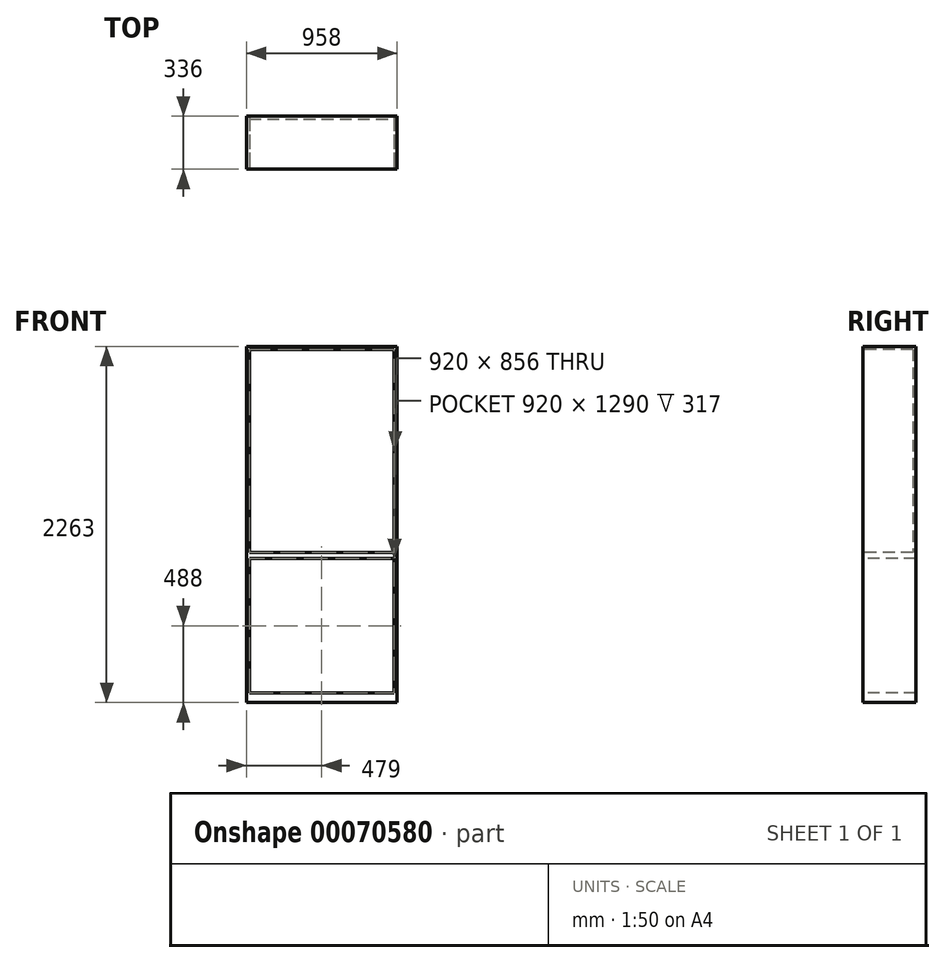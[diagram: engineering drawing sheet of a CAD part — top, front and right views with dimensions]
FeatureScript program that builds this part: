
annotation { "Feature Type Name" : "Feature", "Feature Type Description" : "" }
export const myFeature = defineFeature(function(context is Context, id is Id, definition is map)
    precondition{}
    {
        {
            var Q0;
            Q0=qCreatedBy(makeId("Front.planeOp"),FACE);
            var sketch = newSketch(context, id + "F0", { "sketchPlane" : qUnion([Q0])});
            skLineSegment(sketch, "E0.bottom", {"start": v(0, 0) * mm, "end": v(958, 0) * mm});
            skLineSegment(sketch, "E0.top", {"start": v(0, 2263) * mm, "end": v(958, 2263) * mm});
            skLineSegment(sketch, "E0.left", {"start": v(0, 0) * mm, "end": v(0, 2263) * mm});
            skLineSegment(sketch, "E0.right", {"start": v(958, 0) * mm, "end": v(958, 2263) * mm});
            skSolve(sketch);
        }
        {
            var Q0;
            Q0=makeQuery(id+"F0.imprint","IMPRINT",FACE,{"disambiguationData":[TD([[makeQuery(id+"F0.imprint","IMPRINT",EDGE,{"derivedFrom":sQuery(id+"F0.wireOp",EDGE,"E0.bottom")}),1.0]])]});
            extrude(context, id + "F1", {"entities" : qUnion([Q0]), "depth" : (355 - 19) * mm});
        }
        {
            var Q0;
            Q0=makeQuery(id+"F1.opExtrude","CAP_FACE",FACE,{"disambiguationData":[OSD([sQuery(id+"F0.wireOp",EDGE,"E0.bottom"),sQuery(id+"F0.wireOp",EDGE,"E0.top"),sQuery(id+"F0.wireOp",EDGE,"E0.left"),sQuery(id+"F0.wireOp",EDGE,"E0.right")])],"isStart":false});
            var sketch = newSketch(context, id + "F2", { "sketchPlane" : qUnion([Q0])});
            skLineSegment(sketch, "E1.bottom", {"start": v(19, 916) * mm, "end": v(939, 916) * mm});
            skLineSegment(sketch, "E1.top", {"start": v(19, 60) * mm, "end": v(939, 60) * mm});
            skLineSegment(sketch, "E1.left", {"start": v(19, 916) * mm, "end": v(19, 60) * mm});
            skLineSegment(sketch, "E1.right", {"start": v(939, 916) * mm, "end": v(939, 60) * mm});
            skLineSegment(sketch, "E2.bottom", {"start": v(19, 2244) * mm, "end": v(939, 2244) * mm});
            skLineSegment(sketch, "E2.top", {"start": v(19, 954) * mm, "end": v(939, 954) * mm});
            skLineSegment(sketch, "E2.left", {"start": v(19, 2244) * mm, "end": v(19, 954) * mm});
            skLineSegment(sketch, "E2.right", {"start": v(939, 2244) * mm, "end": v(939, 954) * mm});
            skSolve(sketch);
        }
        {
            var Q0;
            Q0 = qSketchRegion(id + "F2", true);
            extrude(context, id + "F3", {"entities" : qUnion([Q0]), "operationType" : NewBodyOperationType.REMOVE, "oppositeDirection" : true, "depth" : (336 - 19) * mm});
        }
        {
            var Q0;
            Q0=makeQuery(id+"F3.boolean.opBoolean","COPY",FACE,{"derivedFrom":makeQuery(id+"F3.opExtrude","CAP_FACE",FACE,{"disambiguationData":[OSD([sQuery(id+"F2.wireOp",EDGE,"E1.bottom"),sQuery(id+"F2.wireOp",EDGE,"E1.top"),sQuery(id+"F2.wireOp",EDGE,"E1.left"),sQuery(id+"F2.wireOp",EDGE,"E1.right")])],"isStart":false})});
            extrude(context, id + "F4", {"entities" : qUnion([Q0]), "operationType" : NewBodyOperationType.REMOVE, "oppositeDirection" : true, "depth" : 25 * mm});
        }
    });
